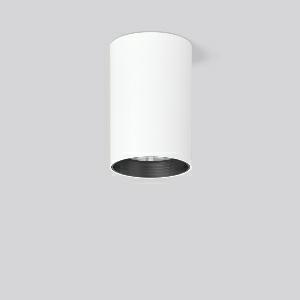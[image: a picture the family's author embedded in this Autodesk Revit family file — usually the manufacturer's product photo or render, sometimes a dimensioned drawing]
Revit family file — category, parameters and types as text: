
# Revit family: heledon_maxi_a_931222_002_2_76_4f2c
name_source: partatom
category: Lighting Fixtures
units: mm (PartAtom-declared; Revit-internal decimal feet)

## family parameters
Cut with Voids When Loaded = No
Host = Face
Light Source = No
Part Type = Normal
Room Calculation Point = No
Round Connector Dimension = Use Diameter
Shared = No

## types (1)
- HELEDON maxi A (1 x LED Modul 927, 2650 lm, 2700)
    Apparent Load = 25 VA
    Approval mark = CE
    CIE Flux Codes = 96 100 100 100 100
    Color Rendering = 92
    Color Temperature = 2700
    Default Elevation = 1800 mm
    Description = Series: HELEDON maxi
Cylindrical surface-mounted downlight. Housing: die-cast aluminium, powder-coated. Internal ceiling frame polycarbonate with bayonet mounting. Black plastic ring and recessed LED to prevent glare from the side. Optical assembly with lens made of plastic (polycarbonate) for the best homogeneous light distribution - can be changed without tools. Best colour rendering index Ra>90. Suitable for Ceiling mounting. Easy installation with a separate ceiling frame with bayonet mounting and plug connection. Driver integrated. Connected via plug-in connector. High quality converter without flickering and stroboscopic effect. The following accessories can be mounted without use of tools: interchangeable lenses, decorative glasses, honeycomb louvre, clear and frosted diffusers, white interchangeable plastic ring. 
Colour: traffic white, matt (RAL 9016)
Diameter: 123 mm
Height: 183 mm
Lamp: LED
Socket: without socket
Colour temperature: 2700K
Colour rendering index (CRI): 92
System power: 25 W
Rated luminous flux: 2650 lm
Luminous efficiency: 106 lm/W
Control gear: Converter, dimmable, DALI
Protection class: I
Type of protection: IP 20
    Height = 183 mm
    Lamp = 1 x LED Modul 927
    Lamp Light Flux = 2650 lm
    Lamp count = 1
    Length = 123 mm
    Lifetime = 50000 h
    Luminous efficacy = 106 lm/W
    Manufacturer = RZB
    ModVariant = No
    Model = 931222.002.2.76
    Mounting Place = Ceiling
    Mounting Type = Surface mounted
    Number of Poles = 1
    OnlyDefault = Yes
    Power Factor = 1
    Product Name = HELEDON maxi A
    Product group = Surface mounted downlights
    ProductGroupID = 302
    Protection Class = Protection class I
    Protection Degree = IP 20
    RLX_Detail_Level = 1
    RLX_Emergency_Light_Flux = 0 lm
    RLX_Emergency_Type = 0
    RLX_Emergency_Type_DB = No
    RlxData = <blob elided: 98993 chars, md5=d5e0fcbd>
    Socket = socket
    Standby Power = 0 W
    System Light Flux = 2650 lm
    System Power = 25 W
    Type Comments = Product without accessories
    Type Image = 931193.002.jpg
    URL = http://relux.com
    VarID = ---
    Voltage = 230 V
    Voltage Range = 220-240 V
    Weight = 0.00 kg
    Width = 0 mm  [stored 0 ft]

note: [stored X ft] marks values corroborated as IEEE doubles in the binary element streams (Revit-internal decimal feet)

## geometry (parser evidence)
native form markers: Blend x4, Sweep x12
no freeform markers — native parametric forms only
